AUTODESK INVENTOR PART (.ipt)
format: ipt  version: 2015 SP1 (Build 190203100, 203)  size: 131,584 bytes
history: native  units: in
note: dims shown in document units (in); Inventor stores cm internally (conversion verified against a paired STEP export)
features: sketch x3, other x1
ambient origin geometry x8: Origin, YZ Plane, XZ Plane, XY Plane, X Axis, Y Axis, Z Axis, Center Point
feature tree (4):
  other  "50cal_geometrysketch.ipt"
  sketch  "Sketch3"  dims[d2=3.2677in d57=2.2425in d58=1.75in d67=0.7543in d70=0.0312in d78=0.8352in d79=0.8352in d80=0.8352in d81=0.8352in d82=0.8352in d83=0.8352in d84=0.0232in d85=0.0075in d87=30.0deg d88=0.5in d89=0.6693in]
  sketch  "Sketch2"  dims[d1=0.7087in]
  sketch  "Sketch1"  dims[d0=0.3937in]
